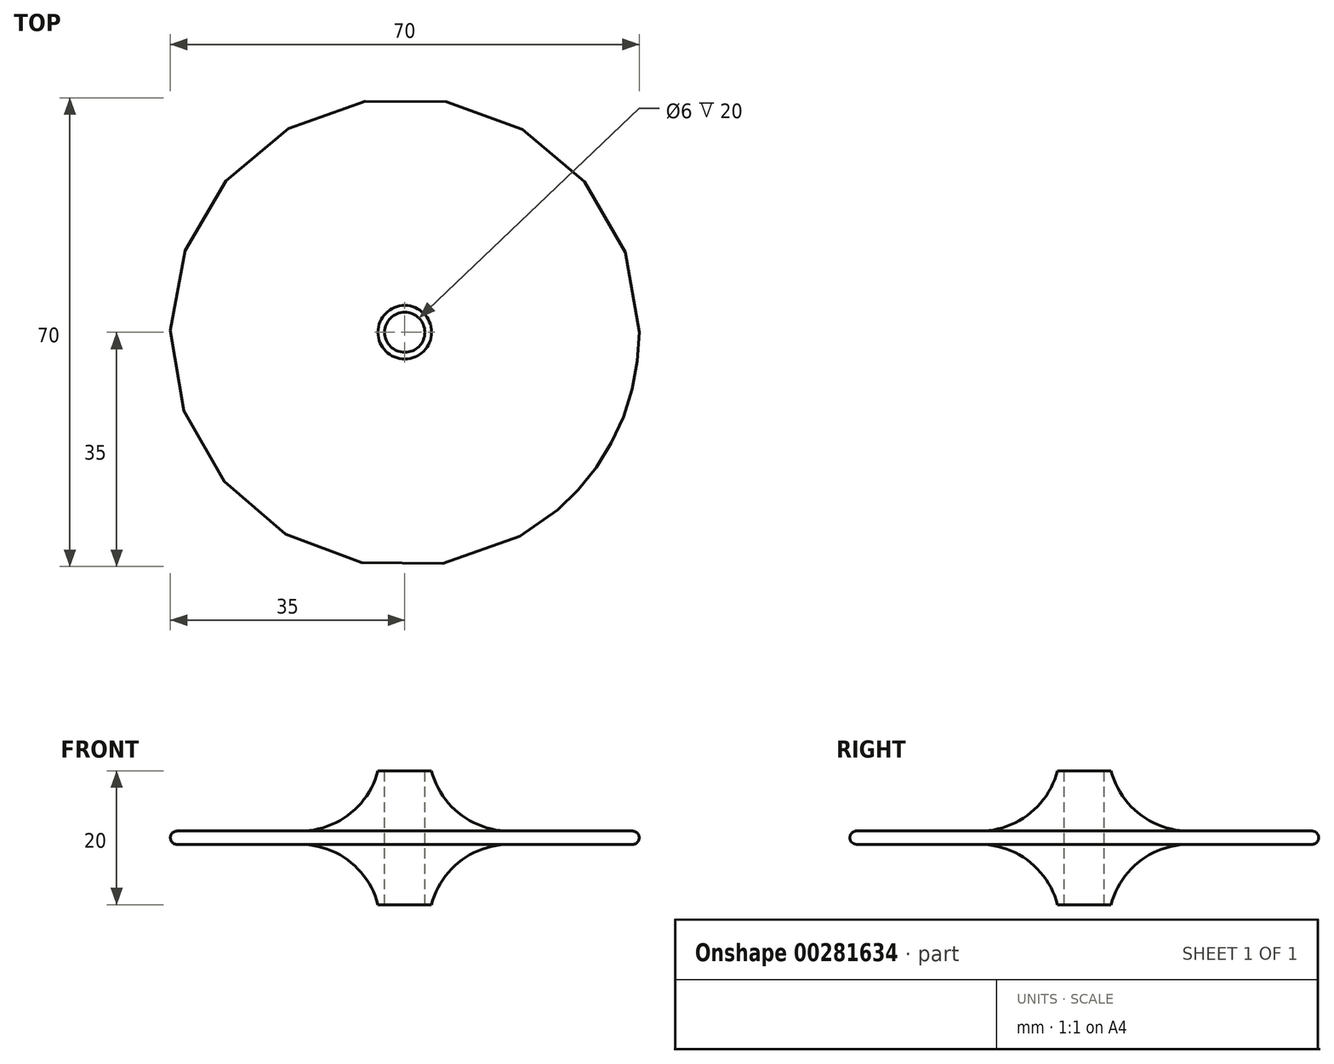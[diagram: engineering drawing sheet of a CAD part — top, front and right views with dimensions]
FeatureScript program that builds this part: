
annotation { "Feature Type Name" : "Feature", "Feature Type Description" : "" }
export const myFeature = defineFeature(function(context is Context, id is Id, definition is map)
    precondition{}
    {
        {
            var Q0;
            Q0=qCreatedBy(makeId("Top.planeOp"),FACE);
            var sketch = newSketch(context, id + "F0", { "sketchPlane" : qUnion([Q0])});
            skCircle(sketch, "E0", {"center": v(0, 0) * mm, "radius": 35 * mm});
            skCircle(sketch, "E1", {"center": v(0, 0) * mm, "radius": 4 * mm});
            skSolve(sketch);
        }
        {
            var Q0;
            Q0=makeQuery(id+"F0.imprint","IMPRINT",FACE,{"disambiguationData":[TD([[makeQuery(id+"F0.imprint","IMPRINT",EDGE,{"derivedFrom":sQuery(id+"F0.wireOp",EDGE,"E1")}),1.0]])]});
            extrude(context, id + "F1", {"entities" : qUnion([Q0]), "endBound" : BoundingType.SYMMETRIC, "depth" : 20 * mm, "offsetDistance" : 25 * mm});
        }
        {
            var Q0;
            Q0=qCreatedBy(makeId("Top.planeOp"),FACE);
            var sketch = newSketch(context, id + "F2", { "sketchPlane" : qUnion([Q0])});
            skCircle(sketch, "E2", {"center": v(0, 0) * mm, "radius": 35 * mm});
            skSolve(sketch);
        }
        {
            var Q0;
            Q0 = qSketchRegion(id + "F2", true);
            extrude(context, id + "F3", {"entities" : qUnion([Q0]), "operationType" : NewBodyOperationType.ADD, "endBound" : BoundingType.SYMMETRIC, "depth" : 2 * mm, "offsetDistance" : 25 * mm});
        }
        {
            var Q0;
            Q0=makeQuery(id+"F3.boolean.opBoolean","INTERSECT",EDGE,{"derivedFrom":[makeQuery(id+"F1.opExtrude","SWEPT_FACE",FACE,{"disambiguationData":[OSD([sQuery(id+"F0.wireOp",EDGE,"E1")])]}),makeQuery(id+"F3.opExtrude","CAP_FACE",FACE,{"disambiguationData":[OSD([sQuery(id+"F2.wireOp",EDGE,"E2")])],"isStart":false})]});
            fillet(context, id + "F4", {"entities" : qUnion([Q0]), "tangentPropagation" : true, "radius" : 12 * mm, "defaultsChanged" : true, "vertexSettings" : []});
        }
        {
            var Q0;
            Q0=makeQuery(id+"F3.boolean.opBoolean","INTERSECT",EDGE,{"derivedFrom":[makeQuery(id+"F1.opExtrude","SWEPT_FACE",FACE,{"disambiguationData":[OSD([sQuery(id+"F0.wireOp",EDGE,"E1")])]}),makeQuery(id+"F3.opExtrude","CAP_FACE",FACE,{"disambiguationData":[OSD([sQuery(id+"F2.wireOp",EDGE,"E2")])],"isStart":true})]});
            fillet(context, id + "F5", {"entities" : qUnion([Q0]), "tangentPropagation" : true, "radius" : 12 * mm, "defaultsChanged" : true, "vertexSettings" : []});
        }
        {
            var Q0;
            Q0=makeQuery(id+"F3.opExtrude","CAP_EDGE",EDGE,{"disambiguationData":[OSD([sQuery(id+"F2.wireOp",EDGE,"E2")])],"isStart":false});
            var Q1;
            Q1=makeQuery(id+"F3.opExtrude","CAP_EDGE",EDGE,{"disambiguationData":[OSD([sQuery(id+"F2.wireOp",EDGE,"E2")])],"isStart":true});
            fillet(context, id + "F6", {"entities" : qUnion([Q0, Q1]), "tangentPropagation" : true, "radius" : 1 * mm, "defaultsChanged" : true, "vertexSettings" : []});
        }
        {
            var Q0;
            Q0=qCreatedBy(makeId("Top.planeOp"),FACE);
            var sketch = newSketch(context, id + "F7", { "sketchPlane" : qUnion([Q0])});
            skCircle(sketch, "E3", {"center": v(0, 0) * mm, "radius": 3 * mm});
            skSolve(sketch);
        }
        {
            var Q0;
            Q0 = qSketchRegion(id + "F7", true);
            extrude(context, id + "F8", {"entities" : qUnion([Q0]), "operationType" : NewBodyOperationType.REMOVE, "endBound" : BoundingType.THROUGH_ALL, "oppositeDirection" : true, "depth" : 25 * mm, "offsetDistance" : 25 * mm});
        }
        {
            var Q0;
            Q0=qCreatedBy(makeId("Top.planeOp"),FACE);
            var sketch = newSketch(context, id + "F9", { "sketchPlane" : qUnion([Q0])});
            skCircle(sketch, "E4", {"center": v(0, 0) * mm, "radius": 3 * mm});
            skSolve(sketch);
        }
        {
            var Q0;
            Q0 = qSketchRegion(id + "F9", true);
            extrude(context, id + "F10", {"entities" : qUnion([Q0]), "operationType" : NewBodyOperationType.REMOVE, "endBound" : BoundingType.THROUGH_ALL, "depth" : 25 * mm, "offsetDistance" : 25 * mm});
        }
    });
